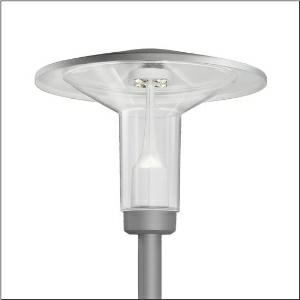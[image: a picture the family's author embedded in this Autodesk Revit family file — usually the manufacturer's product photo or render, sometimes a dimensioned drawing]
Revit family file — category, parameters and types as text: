
# Revit family: laterne_iq___p1_0a_5xa5255ff14h_2151
name_source: partatom
category: Lighting Fixtures
units: mm (PartAtom-declared; Revit-internal decimal feet)

## family parameters
Cut with Voids When Loaded = No
Host = Face
Light Source = No
Part Type = Normal
Room Calculation Point = No
Round Connector Dimension = Use Diameter
Shared = No

## types (1)
- --- (1 x LED, 1510 lm, 10.5 W, 3000K)
    Apparent Load = 11 VA
    CIE Flux Codes = 35 64 91 96 100
    Color Rendering = 70
    Color Temperature = 3000K
    Default Elevation = 1800 mm
    Description = Lantern iQ, mast luminaire, Module 540 iQ-SR, primary light control with 3 zone facetted reflector, of plastic, silver coated, highly specular, structured, primary optical cover: cover, of PMMA, transparent, light distribution: P1.0a, light emission: direct distribution, primary light characteristic: strongly asymmetric, installation type: post-top, LED, High Power LED, rated luminous flux: 1.510lm, luminous efficacy: 144lm/W, light colour: 730, colour temperature: 3000K, control gear: iQ Street-Remote, control: Auto-Match, Temp-Guard, Lumen-Switch, Night-Set, Smart-Wire, Light-Fading, Desk-Remote (wireless, voltage-free reading and setting of iQ features in the workshop via application-optimized NFC function/RFID function), optimised constant luminous flux control (CLO 2.0), Street-Remote, pre-setting: logarithmic dimming characteristic, with terminal, 6-pole, max. 2.5mm², mains connection: 230..240V, AC, 50/60Hz, start of lifetime: 11W, end of service life: 11W, reduction: 5W, luminaire housing, upper part, of glass-fibre reinforced polyester, coated, Siteco® metallic grey (DB 702S), diameter: 750mm, height: 583mm, spigot size: d x l = 76 x 70mm (post-top) | with reducer (optional accessory) 60 x 70mm, mounting height: 3..5m, post-top mast mounting element, of diecast aluminium, coated, Siteco® metallic grey (DB 702S), Module 540 iQ-SR, traffic white (RAL 9016), equipment: standard, protection rating (complete): IP65, insulation class (complete): insulation class II (safety insulation), certification: CE, ENEC, VDE, packaging unit: 1 piece

Light Distribution: P1.0a
    Height = 583 mm
    Lamp = 1 x LED
    Lamp Light Flux = 1510 lm
    Lamp Power = 10.5 W
    Lamp count = 1
    Length = 750 mm
    Luminous efficacy = 144 lm/W
    Manufacturer = Siteco
    ModVariant = No
    Model = 5XA5255FF14H
    Number of Poles = 1
    OnlyDefault = Yes
    Power Factor = 1
    Product Name = Laterne iQ | P1.0a
    Product group = mast luminaire | pylon top
    ProductGroupID = 6100
    Protection Class = Protection class II
    Protection Degree = IP 65
    RLX_Detail_Level = 1
    RLX_Emergency_Light_Flux = 0 lm
    RLX_Emergency_Type = 0
    RLX_Emergency_Type_DB = No
    RlxData = <blob elided: 74001 chars, md5=bd0d4b72>
    Socket = socket
    Standby Power = 0 W
    System Light Flux = 1510 lm
    System Power = 11 W
    Type Comments = factory setting: luminous flux: 100 % | dim-lin: 254 | 419 mA
    Type Image = l_1006050.jpg
    URL = http://relux.com
    VarID = @adj_159983
    Voltage = 0 V
    Weight = 0.00 kg
    Width = 0 mm  [stored 0 ft]

note: [stored X ft] marks values corroborated as IEEE doubles in the binary element streams (Revit-internal decimal feet)

## geometry (parser evidence)
native form markers: Blend x4, Sweep x12
no freeform markers — native parametric forms only
